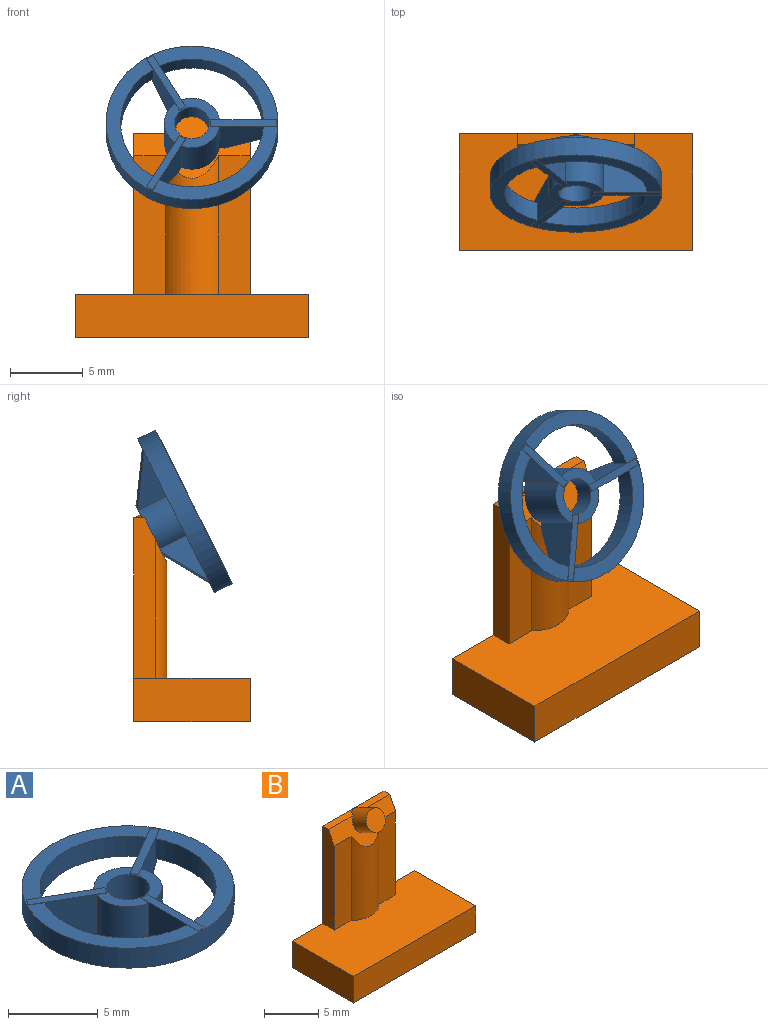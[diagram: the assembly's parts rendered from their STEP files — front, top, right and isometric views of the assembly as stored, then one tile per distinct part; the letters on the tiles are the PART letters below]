
ASSEMBLY  parts=2 mates=1
PART A: 33 faces, bbox 11.8x11.8x3.5 mm
  f0: plane 0.43x0.25mm, normal (-0.87,0.5,0), area 0mm2, adj f1,f2,f4,f28
  f1: plane 3.92x3.52mm, normal (-0.5,-0.87,0), area 8.5mm2, adj f0,f3,f4,f5,f6,f7,f17,f18
  f2: plane 3.92x3.52mm, normal (0.5,0.87,0), area 8.5mm2, adj f0,f3,f4,f5,f6,f7,f8,f9
  f3: plane 0.43x0.25mm, normal (-0.87,0.5,0), area 0mm2, adj f1,f2,f7,f29
  f4: plane 3.58x2.36mm, normal (-0.42,0.24,-0.87), area 2.2mm2, adj f0,f1,f2,f5
  f5: plane 3.86x3.8mm, normal (0,0,-1), area 6.9mm2, adj f1,f2,f4,f9,f11,f12,f14,f18
  f6: plane 0.43x0.25mm, normal (0.87,-0.5,0), area 0mm2, adj f1,f2,f7,f32
  f7: plane 4.17x2.69mm, normal (0,0,1), area 2.3mm2, adj f1,f2,f3,f6
  f8: cylinder r=4.9mm len=8.23mm, axis (0,0,1), area 13.2mm2, adj f2,f19,f28,f29
  f9: cylinder r=1.9mm len=3.5mm, axis (0,0,-1), area 12.2mm2, adj f2,f5,f19,f32
  f10: plane 0.5x0.01mm, normal (0,-1,0), area 0mm2, adj f11,f12,f14,f28
  f11: plane 4.52x3.52mm, normal (1,0,0), area 8.5mm2, adj f5,f10,f13,f14,f15,f16,f26,f28
  f12: plane 4.52x3.52mm, normal (-1,0,0), area 8.5mm2, adj f5,f10,f13,f14,f15,f16,f17,f18
  f13: plane 0.5x0.02mm, normal (0,-1,0), area 0mm2, adj f11,f12,f16,f29
  f14: plane 3.84x2.14mm, normal (0,-0.49,-0.87), area 2.2mm2, adj f5,f10,f11,f12
  f15: plane 0.5x0.02mm, normal (0,1,0), area 0mm2, adj f11,f12,f16,f32
  f16: plane 4.52x0.5mm, normal (0,0,1), area 2.3mm2, adj f11,f12,f13,f15
  f17: cylinder r=4.9mm len=7.12mm, axis (0,0,1), area 13.2mm2, adj f1,f12,f28,f29
  f18: cylinder r=1.9mm len=3.5mm, axis (0,0,-1), area 12.2mm2, adj f1,f5,f12,f32
  f19: plane 3.92x3.52mm, normal (-0.5,0.87,0), area 8.5mm2, adj f5,f8,f9,f21,f22,f23,f24,f25
  f20: plane 3.92x3.52mm, normal (0.5,-0.87,0), area 8.5mm2, adj f5,f21,f22,f23,f24,f25,f26,f28
  f21: plane 0.43x0.25mm, normal (0.87,0.5,0), area 0mm2, adj f19,f20,f23,f28
  f22: plane 0.43x0.25mm, normal (0.87,0.5,0), area 0mm2, adj f19,f20,f25,f29
  f23: plane 3.58x2.36mm, normal (0.42,0.24,-0.87), area 2.2mm2, adj f5,f19,f20,f21
  f24: plane 0.43x0.25mm, normal (-0.87,-0.5,0), area 0mm2, adj f19,f20,f25,f32
  f25: plane 4.17x2.69mm, normal (0,0,1), area 2.3mm2, adj f19,f20,f22,f24
  f26: cylinder r=4.9mm len=7.12mm, axis (0,0,1), area 13.2mm2, adj f11,f20,f28,f29
  f27: cylinder r=5.9mm len=11.8mm, axis (0,0,1), area 50mm2, adj f28,f29
  f28: plane 11.8x11.8mm, normal (0,0,-1), area 32.6mm2, adj f0,f1,f2,f8,f10,f11,f12,f17
  f29: plane 11.8x11.8mm, normal (0,0,1), area 32.6mm2, adj f1,f2,f3,f8,f11,f12,f13,f17
  f30: cylinder r=1.2mm len=3.5mm, axis (0,0,-1), area 26.4mm2, adj f5,f32
  f31: cylinder r=1.9mm len=3.5mm, axis (0,0,-1), area 12.2mm2, adj f5,f11,f20,f32
  f32: plane 3.8x3.78mm, normal (0,0,1), area 5.9mm2, adj f1,f2,f6,f9,f11,f12,f15,f18
PART B: 24 faces, bbox 16x8x15.2 mm
  f0: plane 8x0.75mm, normal (0,0,1), area 5.2mm2, adj f2,f18,f19,f21,f23
  f1: plane 16x8mm, normal (0,0,-1), area 44mm2, adj f2,f3,f4,f5,f7,f8,f9,f10
  f2: plane 16x14mm, normal (0,1,0), area 136mm2, adj f0,f1,f3,f5,f6,f18,f19
  f3: plane 8x3mm, normal (-1,0,0), area 24mm2, adj f1,f2,f4,f6
  f4: plane 16x3mm, normal (0,-1,0), area 48mm2, adj f1,f3,f5,f6
  f5: plane 8x3mm, normal (1,0,0), area 24mm2, adj f1,f2,f4,f6
  f6: plane 16x8mm, normal (0,0,1), area 114.1mm2, adj f2,f3,f4,f5,f16,f17,f18,f19
  f7: plane 14x2mm, normal (0,-1,0), area 28mm2, adj f1,f8,f10,f11
  f8: plane 6x2mm, normal (1,0,0), area 12mm2, adj f1,f7,f9,f11
  f9: plane 14x2mm, normal (0,1,0), area 28mm2, adj f1,f8,f10,f11
  f10: plane 6x2mm, normal (-1,0,0), area 12mm2, adj f1,f7,f9,f11
  f11: plane 14x6mm, normal (0,0,-1), area 76.9mm2, adj f7,f8,f9,f10,f13
  f12: cylinder r=0.8mm len=2mm, axis (0,0,1), area 10.1mm2, adj f14,f15
  f13: cylinder r=1.5mm len=3mm, axis (0,0,1), area 18.8mm2, adj f11,f14
  f14: plane 3x3mm, normal (0,0,-1), area 5.1mm2, adj f12,f13
  f15: plane 1.6x1.6mm, normal (0,0,-1), area 2mm2, adj f12
  f16: cylinder r=2.5mm len=9.5mm, axis (0,0,-1), area 34.3mm2, adj f6,f17,f20,f21
  f17: plane 9.5x2.19mm, normal (0,-1,0), area 20.8mm2, adj f6,f16,f18,f21
  f18: plane 11x1.5mm, normal (1,0,0), area 15.9mm2, adj f0,f2,f6,f17,f21
  f19: plane 11x1.5mm, normal (-1,0,0), area 15.9mm2, adj f0,f2,f6,f20,f21
  f20: plane 9.5x2.19mm, normal (0,-1,0), area 20.8mm2, adj f6,f16,f19,f21
  f21: plane 8x3.05mm, normal (0,-0.89,0.45), area 13.9mm2, adj f0,f16,f17,f18,f19,f20,f23
  f22: plane 2.3x2.06mm, normal (0,-0.89,0.45), area 4.2mm2, adj f23
  f23: cylinder r=1.15mm len=3.38mm, axis (0,-0.89,0.45), area 15.2mm2, adj f0,f21,f22
PLACE A rot(axis=(0.47,-0.47,0.75),106deg) t=(0,1.09,14.14)mm
PLACE B t=(0,-1.92,0.96)mm
MATE fastened B.f23 <-> A.f8  axis (0,-0.89,0.45) through (0,-0.84,15.11)mm
